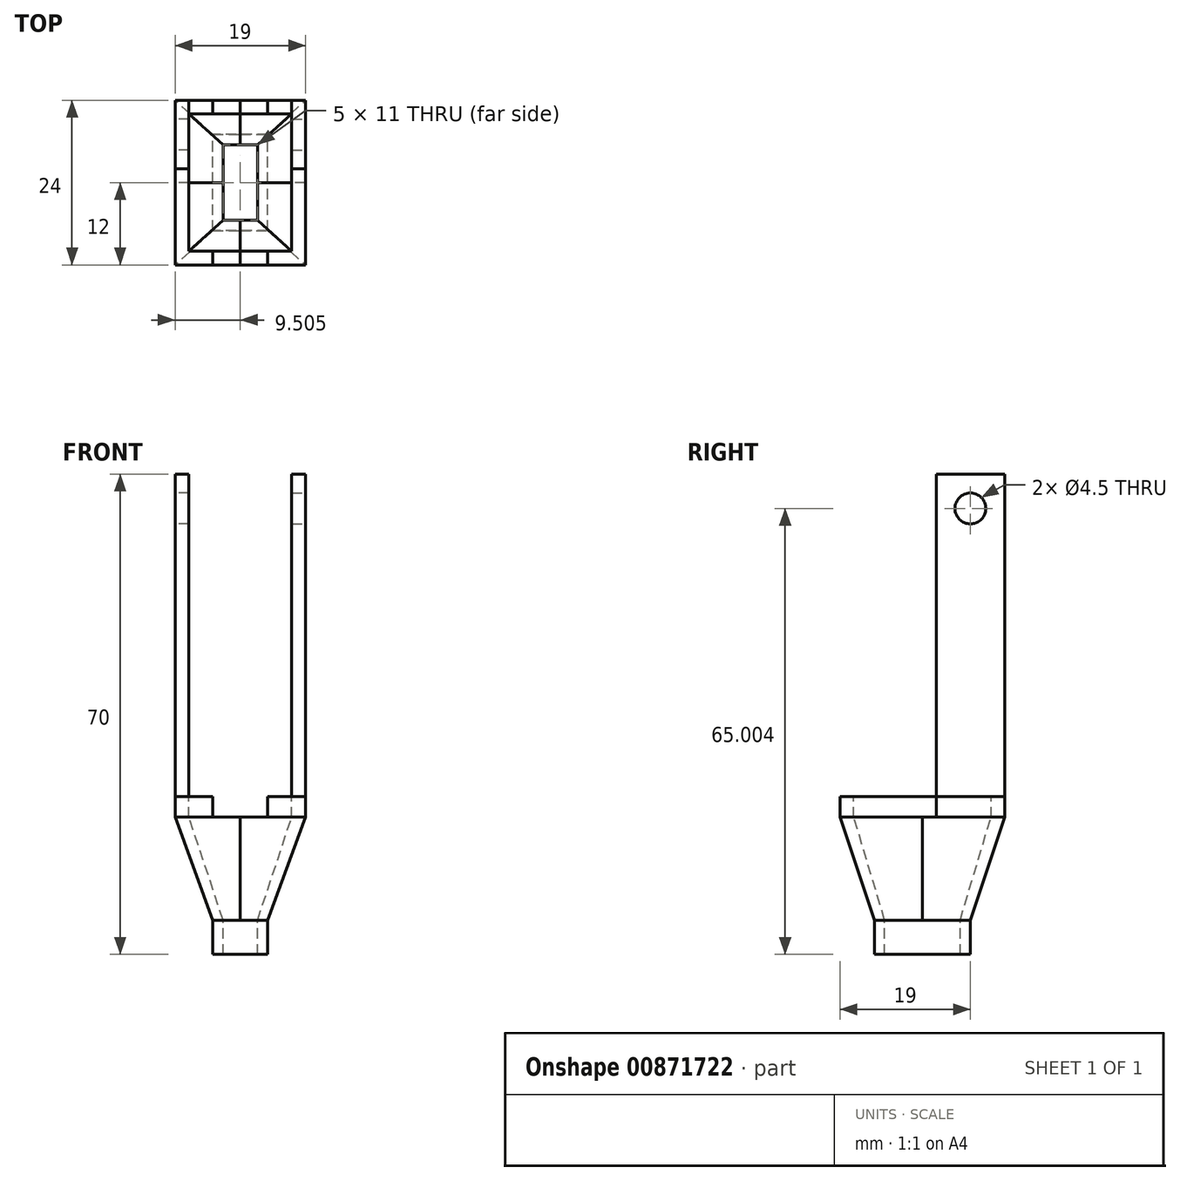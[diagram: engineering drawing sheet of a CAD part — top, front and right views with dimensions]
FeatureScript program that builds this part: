
annotation { "Feature Type Name" : "Feature", "Feature Type Description" : "" }
export const myFeature = defineFeature(function(context is Context, id is Id, definition is map)
    precondition{}
    {
        {
            var Q0;
            Q0=qCreatedBy(makeId("Front.planeOp"),FACE);
            var sketch = newSketch(context, id + "F0", { "sketchPlane" : qUnion([Q0])});
            skLineSegment(sketch, "E0.bottom", {"start": v(-37.07, 27.09) * mm, "end": v(39.37, 27.09) * mm});
            skLineSegment(sketch, "E0.top", {"start": v(-37.07, -34.57) * mm, "end": v(39.37, -34.57) * mm});
            skLineSegment(sketch, "E0.left", {"start": v(-37.07, 27.09) * mm, "end": v(-37.07, -34.57) * mm});
            skLineSegment(sketch, "E0.right", {"start": v(39.37, 27.09) * mm, "end": v(39.37, -34.57) * mm});
            skLineSegment(sketch, "E1.bottom", {"start": v(-20.42, 12.04) * mm, "end": v(-1.42, 12.04) * mm});
            skLineSegment(sketch, "E1.top", {"start": v(-20.42, 9.04) * mm, "end": v(-1.42, 9.04) * mm});
            skLineSegment(sketch, "E1.left", {"start": v(-20.42, 12.04) * mm, "end": v(-20.42, 9.04) * mm});
            skLineSegment(sketch, "E1.right", {"start": v(-1.42, 12.04) * mm, "end": v(-1.42, 9.04) * mm});
            skLineSegment(sketch, "E2", {"start": v(-10.92, 9.04) * mm, "end": v(-10.92, -5.96) * mm});
            skLineSegment(sketch, "E3", {"start": v(-10.92, -5.96) * mm, "end": v(-14.92, -5.96) * mm});
            skLineSegment(sketch, "E4", {"start": v(-14.92, -5.96) * mm, "end": v(-14.92, -10.96) * mm});
            skLineSegment(sketch, "E5.MirrorCS", {"start": v(-10.92, -5.96) * mm, "end": v(-6.92, -5.96) * mm});
            skLineSegment(sketch, "E6.MirrorCS", {"start": v(-6.92, -5.96) * mm, "end": v(-6.92, -10.96) * mm});
            skLineSegment(sketch, "E7", {"start": v(-6.92, -10.96) * mm, "end": v(-14.92, -10.96) * mm});
            skSolve(sketch);
        }
        {
            var Q0;
            Q0=makeQuery(id+"F0.imprint","IMPRINT",FACE,{"disambiguationData":[TD([[makeQuery(id+"F0.imprint","IMPRINT",EDGE,{"derivedFrom":sQuery(id+"F0.wireOp",EDGE,"E1.bottom")}),-1.0]])]});
            var Q1;
            Q1=makeQuery(id+"F0.imprint","IMPRINT",FACE,{"disambiguationData":[TD([[makeQuery(id+"F0.imprint","IMPRINT",EDGE,{"derivedFrom":sQuery(id+"F0.wireOp",EDGE,"E3")}),1.0]])]});
            extrude(context, id + "F1", {"entities" : qUnion([Q0, Q1]), "depth" : 40 * mm, "offsetDistance" : 25 * mm});
        }
        {
            var Q0;
            Q0=makeQuery(id+"F1.opExtrude","SWEPT_FACE",FACE,{"disambiguationData":[OSD([sQuery(id+"F0.wireOp",EDGE,"E1.top")])]});
            var sketch = newSketch(context, id + "F2", { "sketchPlane" : qUnion([Q0])});
            skLineSegment(sketch, "E8", {"start": v(-1.42, 20) * mm, "end": v(-20.42, 20) * mm});
            skLineSegment(sketch, "E9.bottom", {"start": v(-3.42, 30) * mm, "end": v(-18.42, 30) * mm});
            skLineSegment(sketch, "E9.top", {"start": v(-3.42, 10) * mm, "end": v(-18.42, 10) * mm});
            skLineSegment(sketch, "E9.left", {"start": v(-3.42, 30) * mm, "end": v(-3.42, 10) * mm});
            skLineSegment(sketch, "E9.right", {"start": v(-18.42, 30) * mm, "end": v(-18.42, 10) * mm});
            skPoint(sketch, "E9.middle", {"position": v(-10.92, 20) * mm});
            skLineSegment(sketch, "E10", {"start": v(-10.92, 30) * mm, "end": v(-10.92, 32) * mm});
            skLineSegment(sketch, "E11.bottom", {"start": v(-10.92, 32) * mm, "end": v(-1.42, 32) * mm});
            skLineSegment(sketch, "E11.top", {"start": v(-10.92, 40) * mm, "end": v(-1.42, 40) * mm});
            skLineSegment(sketch, "E11.left", {"start": v(-10.92, 32) * mm, "end": v(-10.92, 40) * mm});
            skLineSegment(sketch, "E11.right", {"start": v(-1.42, 32) * mm, "end": v(-1.42, 40) * mm});
            skLineSegment(sketch, "E12.bottom", {"start": v(-10.92, 32) * mm, "end": v(-20.42, 32) * mm});
            skLineSegment(sketch, "E12.top", {"start": v(-10.92, 40) * mm, "end": v(-20.42, 40) * mm});
            skLineSegment(sketch, "E12.right", {"start": v(-20.42, 32) * mm, "end": v(-20.42, 40) * mm});
            skLineSegment(sketch, "E13.MirrorCS", {"start": v(-10.92, 10) * mm, "end": v(-10.92, 8) * mm});
            skLineSegment(sketch, "E14.MirrorCS", {"start": v(-10.92, 8) * mm, "end": v(-1.42, 8) * mm});
            skLineSegment(sketch, "E15.MirrorCS", {"start": v(-10.92, 8) * mm, "end": v(-20.42, 8) * mm});
            skLineSegment(sketch, "E16.MirrorCS", {"start": v(-20.42, 8) * mm, "end": v(-20.42, 0) * mm});
            skLineSegment(sketch, "E17.MirrorCS", {"start": v(-10.92, 0) * mm, "end": v(-20.42, 0) * mm});
            skLineSegment(sketch, "E18.MirrorCS", {"start": v(-10.92, 0) * mm, "end": v(-1.42, 0) * mm});
            skLineSegment(sketch, "E19.MirrorCS", {"start": v(-1.42, 8) * mm, "end": v(-1.42, 0) * mm});
            skSolve(sketch);
        }
        {
            var Q0;
            Q0=makeQuery(id+"F1.opExtrude","SWEPT_FACE",FACE,{"disambiguationData":[OSD([sQuery(id+"F0.wireOp",EDGE,"E7")])]});
            var sketch = newSketch(context, id + "F3", { "sketchPlane" : qUnion([Q0])});
            skLineSegment(sketch, "E20", {"start": v(-6.92, 20) * mm, "end": v(-14.92, 20) * mm});
            skLineSegment(sketch, "E21.bottom", {"start": v(-6.92, 27) * mm, "end": v(-14.92, 27) * mm});
            skLineSegment(sketch, "E21.top", {"start": v(-6.92, 13) * mm, "end": v(-14.92, 13) * mm});
            skLineSegment(sketch, "E21.left", {"start": v(-6.92, 27) * mm, "end": v(-6.92, 13) * mm});
            skLineSegment(sketch, "E21.right", {"start": v(-14.92, 27) * mm, "end": v(-14.92, 13) * mm});
            skPoint(sketch, "E21.middle", {"position": v(-10.92, 20) * mm});
            skSolve(sketch);
        }
        {
            var Q0;
            {var subQ0=sQuery(id+"F3.wireOp",EDGE,"E21.bottom");Q0=makeQuery(id+"F3.imprint","IMPRINT",FACE,{"disambiguationData":[TD([[makeQuery(id+"F3.imprint","IMPRINT",EDGE,{"derivedFrom":subQ0}),-1.0]])]});}
            var Q1;
            {var subQ0=sQuery(id+"F3.wireOp",EDGE,"E21.top");Q1=makeQuery(id+"F3.imprint","IMPRINT",FACE,{"disambiguationData":[TD([[makeQuery(id+"F3.imprint","IMPRINT",EDGE,{"derivedFrom":subQ0}),1.0]])]});}
            extrude(context, id + "F4", {"entities" : qUnion([Q0, Q1]), "operationType" : NewBodyOperationType.REMOVE, "oppositeDirection" : true, "depth" : 25 * mm, "offsetDistance" : 25 * mm});
        }
        {
            var Q0;
            Q0=makeQuery(id+"F2.imprint","IMPRINT",FACE,{"disambiguationData":[TD([[makeQuery(id+"F2.imprint","IMPRINT",EDGE,{"derivedFrom":sQuery(id+"F2.wireOp",EDGE,"E11.bottom")}),1.0]])]});
            var Q1;
            Q1=makeQuery(id+"F2.imprint","IMPRINT",FACE,{"disambiguationData":[TD([[makeQuery(id+"F2.imprint","IMPRINT",EDGE,{"derivedFrom":sQuery(id+"F2.wireOp",EDGE,"E12.bottom")}),-1.0]])]});
            var Q2;
            Q2=makeQuery(id+"F2.imprint","IMPRINT",FACE,{"disambiguationData":[TD([[makeQuery(id+"F2.imprint","IMPRINT",EDGE,{"derivedFrom":sQuery(id+"F2.wireOp",EDGE,"E14.MirrorCS")}),-1.0]])]});
            extrude(context, id + "F5", {"entities" : qUnion([Q0, Q1, Q2]), "operationType" : NewBodyOperationType.REMOVE, "oppositeDirection" : true, "depth" : 25 * mm, "offsetDistance" : 25 * mm});
        }
        {
            var Q0;
            Q0=makeQuery(id+"F1.opExtrude","SWEPT_FACE",FACE,{"disambiguationData":[OSD([sQuery(id+"F0.wireOp",EDGE,"E3"),sQuery(id+"F0.wireOp",EDGE,"E5.MirrorCS")])]});
            var sketch = newSketch(context, id + "F6", { "sketchPlane" : qUnion([Q0])});
            skLineSegment(sketch, "E22", {"start": v(-10.92, -27) * mm, "end": v(-10.92, -25.5) * mm});
            skLineSegment(sketch, "E23", {"start": v(-10.92, -13) * mm, "end": v(-10.92, -14.5) * mm});
            skLineSegment(sketch, "E24", {"start": v(-6.92, -20) * mm, "end": v(-8.42, -20) * mm});
            skLineSegment(sketch, "E25.MirrorCS", {"start": v(-14.92, -20) * mm, "end": v(-13.42, -20) * mm});
            skLineSegment(sketch, "E26", {"start": v(-14.92, -20) * mm, "end": v(-6.92, -20) * mm});
            skLineSegment(sketch, "E27.bottom", {"start": v(-13.42, -20) * mm, "end": v(-10.92, -20) * mm});
            skLineSegment(sketch, "E27.top", {"start": v(-13.42, -25.5) * mm, "end": v(-10.92, -25.5) * mm});
            skLineSegment(sketch, "E27.left", {"start": v(-13.42, -20) * mm, "end": v(-13.42, -25.5) * mm});
            skLineSegment(sketch, "E27.right", {"start": v(-10.92, -20) * mm, "end": v(-10.92, -25.5) * mm});
            skLineSegment(sketch, "E28.bottom", {"start": v(-10.92, -25.5) * mm, "end": v(-8.42, -25.5) * mm});
            skLineSegment(sketch, "E28.top", {"start": v(-10.92, -20) * mm, "end": v(-8.42, -20) * mm});
            skLineSegment(sketch, "E28.left", {"start": v(-10.92, -25.5) * mm, "end": v(-10.92, -20) * mm});
            skLineSegment(sketch, "E28.right", {"start": v(-8.42, -25.5) * mm, "end": v(-8.42, -20) * mm});
            skLineSegment(sketch, "E29.bottom", {"start": v(-10.92, -14.5) * mm, "end": v(-13.42, -14.5) * mm});
            skLineSegment(sketch, "E29.top", {"start": v(-10.92, -20) * mm, "end": v(-13.42, -20) * mm});
            skLineSegment(sketch, "E29.left", {"start": v(-10.92, -14.5) * mm, "end": v(-10.92, -20) * mm});
            skLineSegment(sketch, "E29.right", {"start": v(-13.42, -14.5) * mm, "end": v(-13.42, -20) * mm});
            skLineSegment(sketch, "E30.bottom", {"start": v(-10.92, -14.5) * mm, "end": v(-8.42, -14.5) * mm});
            skLineSegment(sketch, "E30.right", {"start": v(-8.42, -14.5) * mm, "end": v(-8.42, -20) * mm});
            skSolve(sketch);
        }
        {
            var Q0;
            {var subQ0=sQuery(id+"F2.wireOp",EDGE,"E9.left");var subQ3=sQuery(id+"F2.wireOp",EDGE,"E8");var subQ4=makeQuery(id+"F2.imprint","INTERSECT",VERTEX,{"derivedFrom":[subQ3,subQ0]});Q0=makeQuery(id+"F2.imprint","IMPRINT",FACE,{"disambiguationData":[TD([[makeQuery(id+"F2.imprint","IMPRINT",EDGE,{"disambiguationData":[TD([[subQ4,-1.0]])],"derivedFrom":subQ3}),1.0]])]});}
            var Q1;
            {var subQ0=sQuery(id+"F2.wireOp",EDGE,"E9.left");var subQ3=sQuery(id+"F2.wireOp",EDGE,"E8");var subQ4=makeQuery(id+"F2.imprint","INTERSECT",VERTEX,{"derivedFrom":[subQ3,subQ0]});Q1=makeQuery(id+"F2.imprint","IMPRINT",FACE,{"disambiguationData":[TD([[makeQuery(id+"F2.imprint","IMPRINT",EDGE,{"disambiguationData":[TD([[subQ4,-1.0]])],"derivedFrom":subQ3}),-1.0]])]});}
            extrude(context, id + "F7", {"entities" : qUnion([Q0, Q1]), "operationType" : NewBodyOperationType.REMOVE, "oppositeDirection" : true, "depth" : 25 * mm, "offsetDistance" : 25 * mm});
        }
        {
            var Q0;
            Q0=makeQuery(id+"F6.imprint","IMPRINT",FACE,{"disambiguationData":[TD([[makeQuery(id+"F6.imprint","IMPRINT",EDGE,{"derivedFrom":sQuery(id+"F6.wireOp",EDGE,"E29.bottom")}),1.0]])]});
            var Q1;
            Q1=makeQuery(id+"F6.imprint","IMPRINT",FACE,{"disambiguationData":[TD([[makeQuery(id+"F6.imprint","IMPRINT",EDGE,{"derivedFrom":sQuery(id+"F6.wireOp",EDGE,"E30.bottom")}),-1.0]])]});
            var Q2;
            Q2=makeQuery(id+"F6.imprint","IMPRINT",FACE,{"disambiguationData":[TD([[makeQuery(id+"F6.imprint","IMPRINT",EDGE,{"derivedFrom":sQuery(id+"F6.wireOp",EDGE,"E28.bottom")}),1.0]])]});
            var Q3;
            Q3=makeQuery(id+"F6.imprint","IMPRINT",FACE,{"disambiguationData":[TD([[makeQuery(id+"F6.imprint","IMPRINT",EDGE,{"derivedFrom":sQuery(id+"F6.wireOp",EDGE,"E27.top")}),1.0]])]});
            extrude(context, id + "F8", {"entities" : qUnion([Q0, Q1, Q2, Q3]), "operationType" : NewBodyOperationType.REMOVE, "oppositeDirection" : true, "depth" : 25 * mm, "offsetDistance" : 25 * mm});
        }
        {
            var Q0;
            {var subQ5=sQuery(id+"F6.wireOp",EDGE,"E23");Q0=makeQuery(id+"F6.imprint","IMPRINT",FACE,{"disambiguationData":[TD([[makeQuery(id+"F6.imprint","IMPRINT",EDGE,{"derivedFrom":subQ5}),-1.0]])]});}
            var Q1;
            {var subQ0=sQuery(id+"F2.wireOp",EDGE,"E13.MirrorCS");Q1=makeQuery(id+"F2.imprint","IMPRINT",FACE,{"disambiguationData":[TD([[makeQuery(id+"F2.imprint","IMPRINT",EDGE,{"derivedFrom":subQ0}),-1.0]])]});}
            loft(context, id + "F9", {"sheetProfilesArray" : [{ "sheetProfileEntities" : qUnion([Q0]) }, { "sheetProfileEntities" : qUnion([Q1]) }]});
        }
        {
            var Q0;
            {var subQ1=sQuery(id+"F6.wireOp",EDGE,"E23");Q0=makeQuery(id+"F6.imprint","IMPRINT",FACE,{"disambiguationData":[TD([[makeQuery(id+"F6.imprint","IMPRINT",EDGE,{"derivedFrom":subQ1}),1.0]])]});}
            var Q1;
            {var subQ0=sQuery(id+"F2.wireOp",EDGE,"E13.MirrorCS");Q1=makeQuery(id+"F2.imprint","IMPRINT",FACE,{"disambiguationData":[TD([[makeQuery(id+"F2.imprint","IMPRINT",EDGE,{"derivedFrom":subQ0}),1.0]])]});}
            loft(context, id + "F10", {"sheetProfilesArray" : [{ "sheetProfileEntities" : qUnion([Q0]) }, { "sheetProfileEntities" : qUnion([Q1]) }]});
        }
        {
            var Q0;
            {var subQ5=sQuery(id+"F6.wireOp",EDGE,"E22");Q0=makeQuery(id+"F6.imprint","IMPRINT",FACE,{"disambiguationData":[TD([[makeQuery(id+"F6.imprint","IMPRINT",EDGE,{"derivedFrom":subQ5}),-1.0]])]});}
            var Q1;
            {var subQ0=sQuery(id+"F2.wireOp",EDGE,"E10");Q1=makeQuery(id+"F2.imprint","IMPRINT",FACE,{"disambiguationData":[TD([[makeQuery(id+"F2.imprint","IMPRINT",EDGE,{"derivedFrom":subQ0}),-1.0]])]});}
            loft(context, id + "F11", {"sheetProfilesArray" : [{ "sheetProfileEntities" : qUnion([Q0]) }, { "sheetProfileEntities" : qUnion([Q1]) }]});
        }
        {
            var Q0;
            {var subQ7=sQuery(id+"F6.wireOp",EDGE,"E22");Q0=makeQuery(id+"F6.imprint","IMPRINT",FACE,{"disambiguationData":[TD([[makeQuery(id+"F6.imprint","IMPRINT",EDGE,{"derivedFrom":subQ7}),1.0]])]});}
            var Q1;
            {var subQ0=sQuery(id+"F2.wireOp",EDGE,"E10");Q1=makeQuery(id+"F2.imprint","IMPRINT",FACE,{"disambiguationData":[TD([[makeQuery(id+"F2.imprint","IMPRINT",EDGE,{"derivedFrom":subQ0}),1.0]])]});}
            loft(context, id + "F12", {"sheetProfilesArray" : [{ "sheetProfileEntities" : qUnion([Q0]) }, { "sheetProfileEntities" : qUnion([Q1]) }]});
        }
        {
            var Q0;
            Q0=makeQuery(id+"F1.opExtrude","SWEPT_FACE",FACE,{"disambiguationData":[OSD([sQuery(id+"F0.wireOp",EDGE,"E1.right")])]});
            var sketch = newSketch(context, id + "F13", { "sketchPlane" : qUnion([Q0])});
            skLineSegment(sketch, "E31.bottom", {"start": v(-8, 9.04) * mm, "end": v(-18, 9.04) * mm});
            skLineSegment(sketch, "E31.top", {"start": v(-8, 59.04) * mm, "end": v(-18, 59.04) * mm});
            skLineSegment(sketch, "E31.left", {"start": v(-8, 9.04) * mm, "end": v(-8, 59.04) * mm});
            skLineSegment(sketch, "E31.right", {"start": v(-18, 9.04) * mm, "end": v(-18, 59.04) * mm});
            skLineSegment(sketch, "E32", {"start": v(-8, 13.6) * mm, "end": v(-13, 13.6) * mm});
            skLineSegment(sketch, "E33", {"start": v(-13, 9.04) * mm, "end": v(-13, 54.04) * mm});
            skCircle(sketch, "E34", {"center": v(-13, 54.04) * mm, "radius": 2.25 * mm});
            skSolve(sketch);
        }
        {
            var Q0;
            Q0 = qSketchRegion(id + "F13", true);
            extrude(context, id + "F14", {"entities" : qUnion([Q0]), "depth" : -2 * mm, "offsetDistance" : 25 * mm});
        }
        {
            var Q0;
            Q0=makeQuery(id+"F1.opExtrude","SWEPT_FACE",FACE,{"disambiguationData":[OSD([sQuery(id+"F0.wireOp",EDGE,"E1.left")])]});
            var sketch = newSketch(context, id + "F15", { "sketchPlane" : qUnion([Q0])});
            skLineSegment(sketch, "E35.bottom", {"start": v(8, 9.04) * mm, "end": v(18, 9.04) * mm});
            skLineSegment(sketch, "E35.top", {"start": v(8, 59.04) * mm, "end": v(18, 59.04) * mm});
            skLineSegment(sketch, "E35.left", {"start": v(8, 9.04) * mm, "end": v(8, 59.04) * mm});
            skLineSegment(sketch, "E35.right", {"start": v(18, 9.04) * mm, "end": v(18, 59.04) * mm});
            skLineSegment(sketch, "E36", {"start": v(13, 9.04) * mm, "end": v(13, 54.04) * mm});
            skCircle(sketch, "E37", {"center": v(13, 54.04) * mm, "radius": 2.25 * mm});
            skSolve(sketch);
        }
        {
            var Q0;
            Q0 = qSketchRegion(id + "F15", true);
            extrude(context, id + "F16", {"entities" : qUnion([Q0]), "depth" : -2 * mm, "offsetDistance" : 25 * mm});
        }
    });
